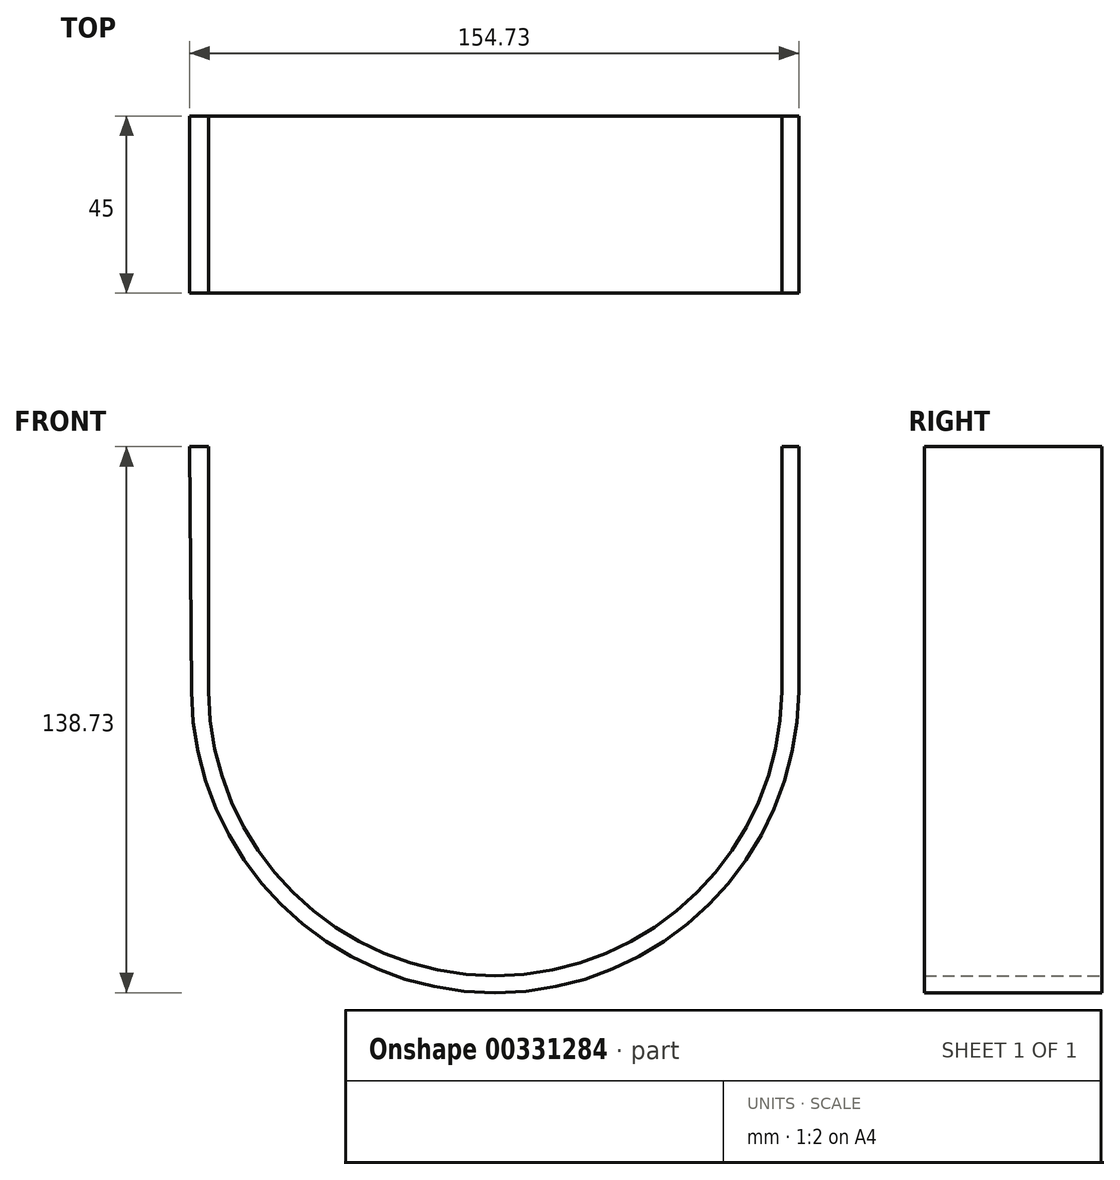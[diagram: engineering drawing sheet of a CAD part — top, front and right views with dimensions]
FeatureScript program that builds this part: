
annotation { "Feature Type Name" : "Feature", "Feature Type Description" : "" }
export const myFeature = defineFeature(function(context is Context, id is Id, definition is map)
    precondition{}
    {
        {
            var Q0;
            Q0=qCreatedBy(makeId("Front.planeOp"),FACE);
            var sketch = newSketch(context, id + "F0", { "sketchPlane" : qUnion([Q0])});
            skArc(sketch, "E0", {"start": v(-77.13, -0.57) * mm, "mid": v(0, -77.13) * mm, "end": v(77.13, -0.57) * mm});
            skArc(sketch, "E1", {"start": v(-72.81, -0.57) * mm, "mid": v(0, -72.82) * mm, "end": v(72.81, -0.57) * mm});
            skLineSegment(sketch, "E2", {"start": v(-77.13, -0.57) * mm, "end": v(-77.6, 61.6) * mm});
            skLineSegment(sketch, "E3.bottom", {"start": v(-77.6, 61.6) * mm, "end": v(-72.81, 61.6) * mm});
            skLineSegment(sketch, "E3.top", {"start": v(-77.6, -0.57) * mm, "end": v(-77.13, -0.57) * mm});
            skLineSegment(sketch, "E3.left", {"start": v(-77.6, 61.6) * mm, "end": v(-77.6, -0.57) * mm});
            skLineSegment(sketch, "E3.right", {"start": v(77.13, 61.6) * mm, "end": v(77.13, -0.57) * mm});
            skLineSegment(sketch, "E4", {"start": v(-72.81, -0.57) * mm, "end": v(-72.81, 61.6) * mm});
            skLineSegment(sketch, "E5", {"start": v(72.81, -0.57) * mm, "end": v(72.81, 61.6) * mm});
            skLineSegment(sketch, "E6.trimOffspring", {"start": v(72.81, 61.6) * mm, "end": v(77.13, 61.6) * mm});
            skSolve(sketch);
        }
        {
            var Q0;
            Q0=makeQuery(id+"F0.imprint","IMPRINT",FACE,{"disambiguationData":[TD([[makeQuery(id+"F0.imprint","IMPRINT",EDGE,{"derivedFrom":sQuery(id+"F0.wireOp",EDGE,"E0")}),1.0]])]});
            var sketch = newSketch(context, id + "F1", { "sketchPlane" : qUnion([Q0])});
            skSolve(sketch);
        }
        {
            var Q0;
            Q0 = qSketchRegion(id + "F1", true);
            var Q1;
            Q1=makeQuery(id+"F0.imprint","IMPRINT",FACE,{"disambiguationData":[TD([[makeQuery(id+"F0.imprint","IMPRINT",EDGE,{"derivedFrom":sQuery(id+"F0.wireOp",EDGE,"E0")}),1.0]])]});
            extrude(context, id + "F2", {"entities" : qUnion([Q0, Q1]), "endBound" : BoundingType.SYMMETRIC, "depth" : 45 * mm, "hasSecondDirection" : true, "secondDirectionOppositeDirection" : true, "secondDirectionDepth" : 25.4 * mm});
        }
    });
